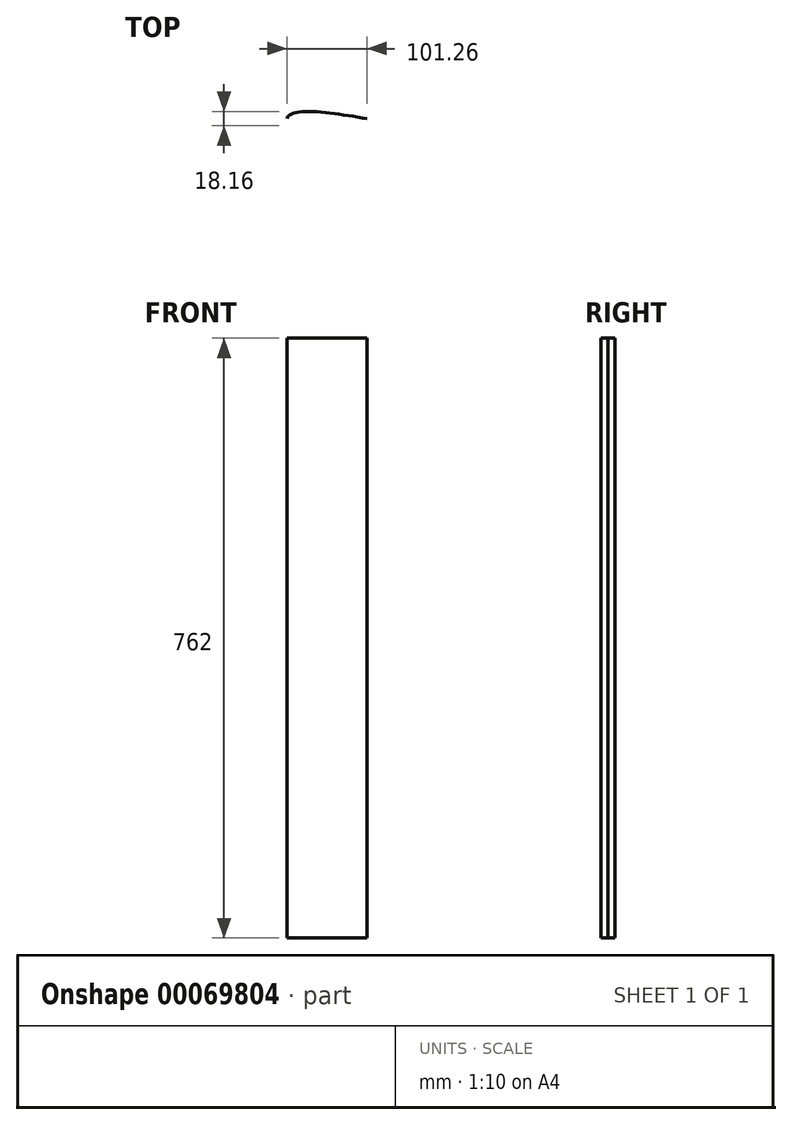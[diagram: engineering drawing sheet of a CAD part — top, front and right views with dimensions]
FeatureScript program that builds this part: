
annotation { "Feature Type Name" : "Feature", "Feature Type Description" : "" }
export const myFeature = defineFeature(function(context is Context, id is Id, definition is map)
    precondition{}
    {
        {
            var Q0;
            Q0=qCreatedBy(makeId("Top.planeOp"),FACE);
            var sketch = newSketch(context, id + "F0", { "sketchPlane" : qUnion([Q0])});
            skFitSpline(sketch, "E0", {"points": [v(0, 0) * mm, v(16.06, 8.48) * mm, v(101.26, 0) * mm], "startDerivative": vector(0, 41.05) * mm, "endDerivative": vector(130.14, -21.63) * mm});
            skLineSegment(sketch, "E1", {"start": v(0, 0) * mm, "end": v(101.26, 0) * mm, "construction": true});
            skFitSpline(sketch, "E2.MirrorCS", {"points": [v(0, 0) * mm, v(16.06, -8.48) * mm, v(101.26, 0) * mm], "startDerivative": vector(0, -41.05) * mm, "endDerivative": vector(130.14, 21.63) * mm});
            skSolve(sketch);
        }
        {
            var Q0;
            Q0=makeQuery(id+"F0.imprint","IMPRINT",FACE,{"disambiguationData":[TD([[makeQuery(id+"F0.imprint","IMPRINT",EDGE,{"derivedFrom":sQuery(id+"F0.wireOp",EDGE,"E0")}),-1.0]])]});
            extrude(context, id + "F1", {"entities" : qUnion([Q0]), "endBound" : BoundingType.SYMMETRIC, "depth" : 762 * mm});
        }
    });
